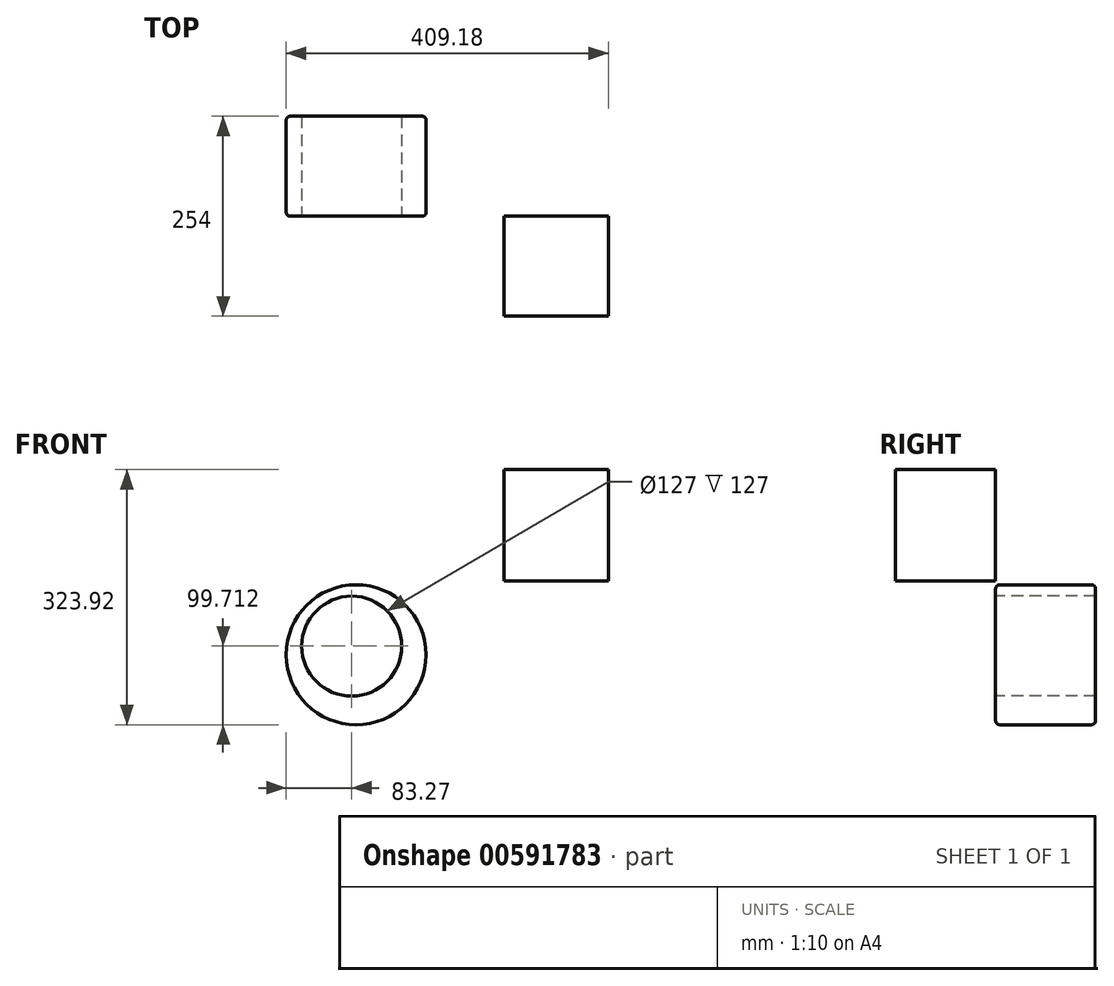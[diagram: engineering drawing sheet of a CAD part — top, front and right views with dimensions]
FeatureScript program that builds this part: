
annotation { "Feature Type Name" : "Feature", "Feature Type Description" : "" }
export const myFeature = defineFeature(function(context is Context, id is Id, definition is map)
    precondition{}
    {
        {
            var Q0;
            Q0=qCreatedBy(makeId("Front.planeOp"),FACE);
            var sketch = newSketch(context, id + "F0", { "sketchPlane" : qUnion([Q0])});
            skCircle(sketch, "E0", {"center": v(5.6, 8.23) * mm, "radius": 88.87 * mm});
            skSolve(sketch);
        }
        {
            var Q0;
            Q0 = qSketchRegion(id + "F0", true);
            extrude(context, id + "F1", {"entities" : qUnion([Q0]), "depth" : 127 * mm, "offsetDistance" : 25.4 * mm});
        }
        {
            var Q0;
            Q0=makeQuery(id+"F1.opExtrude","CAP_EDGE",EDGE,{"disambiguationData":[OSD([sQuery(id+"F0.wireOp",EDGE,"E0")])],"isStart":false});
            var Q1;
            Q1=makeQuery(id+"F1.opExtrude","CAP_FACE",FACE,{"disambiguationData":[OSD([sQuery(id+"F0.wireOp",EDGE,"E0")])],"isStart":false});
            var Q2;
            Q2=makeQuery(id+"F1.opExtrude","SWEPT_FACE",FACE,{"disambiguationData":[OSD([sQuery(id+"F0.wireOp",EDGE,"E0")])]});
            fillet(context, id + "F2", {"entities" : qUnion([Q0, Q1, Q2]), "radius" : 5.08 * mm, "tangentPropagation" : true, "allowEdgeOverflow" : false});
        }
        {
            var Q0;
            Q0=makeQuery(id+"F1.opExtrude","CAP_FACE",FACE,{"disambiguationData":[OSD([sQuery(id+"F0.wireOp",EDGE,"E0")])],"isStart":false});
            var sketch = newSketch(context, id + "F3", { "sketchPlane" : qUnion([Q0])});
            skPoint(sketch, "E1", {"position": v(0, 19.07) * mm});
            skSolve(sketch);
        }
        {
            var Q0;
            Q0=sQuery(id+"F3.wireOp",VERTEX,"E1");
            var Q1;
            Q1=makeQuery(id+"F1.opExtrude","SWEPT_BODY",BODY,{"disambiguationData":[OSD([sQuery(id+"F0.wireOp",EDGE,"E0")])]});
            hole(context, id + "F4", {"style" : HoleStyle.SIMPLE, "endStyle" : HoleEndStyle.THROUGH, "holeDiameter" : 127 * mm, "majorDiameter" : 6.35 * mm, "isTappedThrough" : true, "tappedDepth" : 12.7 * mm, "tapClearance" : 3, "locations" : qUnion([Q0]), "scope" : qUnion([Q1])});
        }
        {
            var Q0;
            Q0=makeQuery(id+"F1.opExtrude","CAP_FACE",FACE,{"disambiguationData":[OSD([sQuery(id+"F0.wireOp",EDGE,"E0")])],"isStart":false});
            var sketch = newSketch(context, id + "F5", { "sketchPlane" : qUnion([Q0])});
            skLineSegment(sketch, "E2.bottom", {"start": v(193.15, 243.28) * mm, "end": v(325.91, 243.28) * mm});
            skLineSegment(sketch, "E2.top", {"start": v(193.15, 101.7) * mm, "end": v(325.91, 101.7) * mm});
            skLineSegment(sketch, "E2.left", {"start": v(193.15, 243.28) * mm, "end": v(193.15, 101.7) * mm});
            skLineSegment(sketch, "E2.right", {"start": v(325.91, 243.28) * mm, "end": v(325.91, 101.7) * mm});
            skSolve(sketch);
        }
        {
            var Q0;
            Q0 = qSketchRegion(id + "F5", true);
            extrude(context, id + "F6", {"entities" : qUnion([Q0]), "depth" : 127 * mm, "offsetDistance" : 25.4 * mm});
        }
    });
